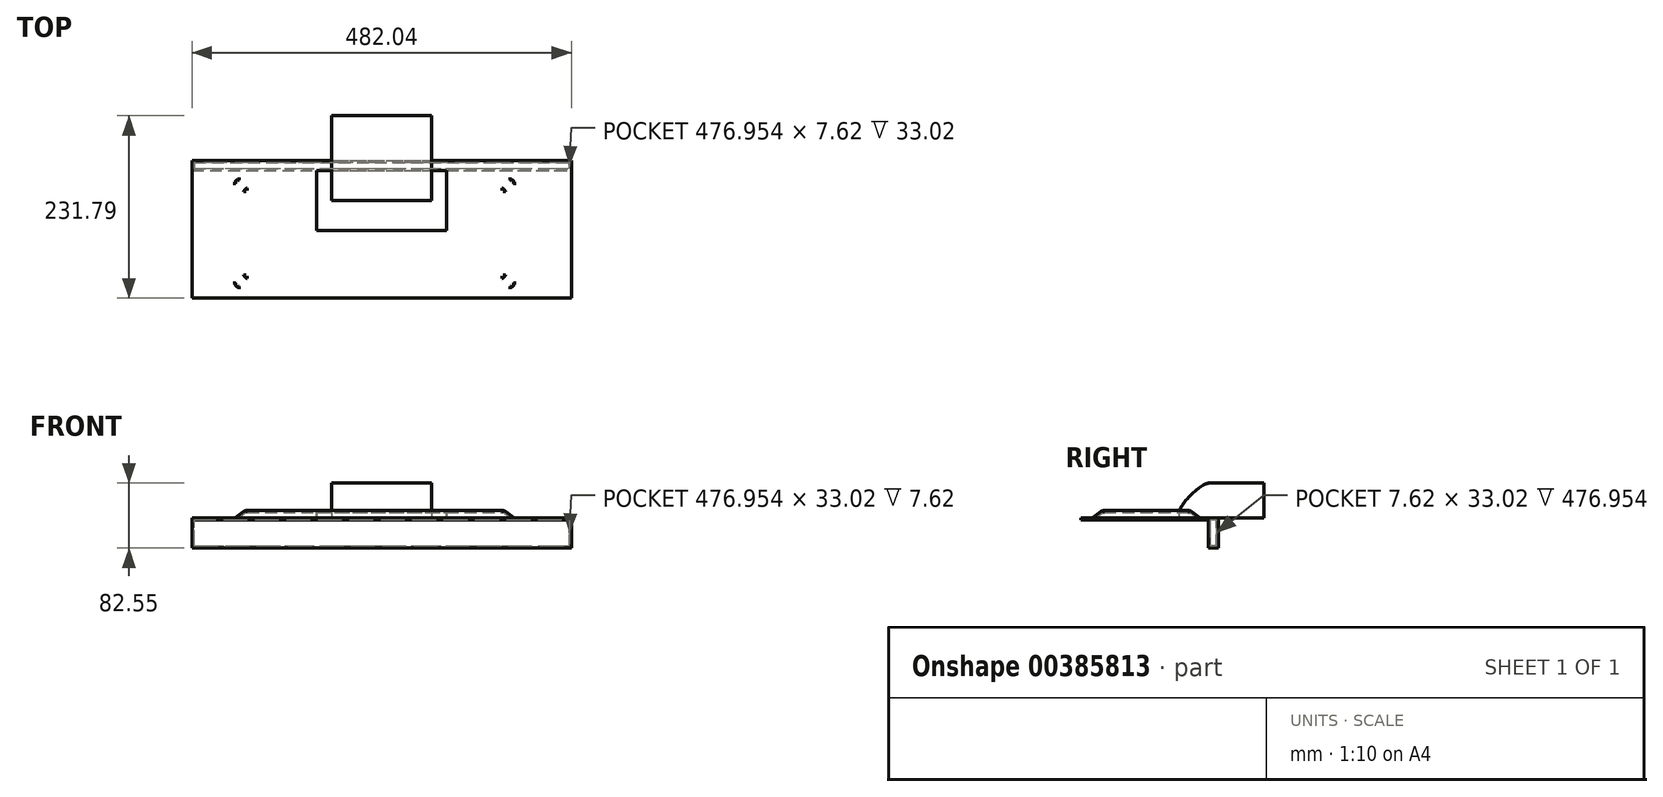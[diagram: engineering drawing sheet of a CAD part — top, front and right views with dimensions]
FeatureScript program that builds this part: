
annotation { "Feature Type Name" : "Feature", "Feature Type Description" : "" }
export const myFeature = defineFeature(function(context is Context, id is Id, definition is map)
    precondition{}
    {
        {
            var Q0;
            Q0=qCreatedBy(makeId("Top.planeOp"),FACE);
            var sketch = newSketch(context, id + "F0", { "sketchPlane" : qUnion([Q0])});
            skLineSegment(sketch, "E0", {"start": v(-241.02, 0) * mm, "end": v(241.02, 0) * mm});
            skLineSegment(sketch, "E1", {"start": v(-241.02, 0) * mm, "end": v(-241.02, -12.7) * mm});
            skLineSegment(sketch, "E2", {"start": v(-241.02, -12.7) * mm, "end": v(241.02, -12.7) * mm});
            skLineSegment(sketch, "E3", {"start": v(241.02, -12.7) * mm, "end": v(241.02, 0) * mm});
            skLineSegment(sketch, "E4", {"start": v(-82.55, -12.7) * mm, "end": v(-82.55, -88.9) * mm});
            skLineSegment(sketch, "E5", {"start": v(-82.55, -88.9) * mm, "end": v(82.55, -88.9) * mm});
            skLineSegment(sketch, "E6", {"start": v(82.55, -88.9) * mm, "end": v(82.55, -12.7) * mm});
            skLineSegment(sketch, "E7", {"start": v(0, -88.9) * mm, "end": v(0, 0) * mm, "construction": true});
            skLineSegment(sketch, "E8", {"start": v(241.02, -12.7) * mm, "end": v(241.02, -174.64) * mm});
            skLineSegment(sketch, "E9", {"start": v(-241.02, -12.7) * mm, "end": v(-241.02, -174.64) * mm});
            skLineSegment(sketch, "E10", {"start": v(-241.02, -174.64) * mm, "end": v(241.02, -174.64) * mm});
            skSolve(sketch);
        }
        {
            var Q0;
            Q0=makeQuery(id+"F0.imprint","IMPRINT",FACE,{"disambiguationData":[TD([[makeQuery(id+"F0.imprint","IMPRINT",EDGE,{"derivedFrom":sQuery(id+"F0.wireOp",EDGE,"E0")}),-1.0]])]});
            extrude(context, id + "F1", {"entities" : qUnion([Q0]), "oppositeDirection" : true, "depth" : 38.1 * mm});
        }
        {
            var Q0;
            {var subQ0=sQuery(id+"F0.wireOp",EDGE,"E4");Q0=makeQuery(id+"F0.imprint","IMPRINT",FACE,{"disambiguationData":[TD([[makeQuery(id+"F0.imprint","IMPRINT",EDGE,{"derivedFrom":subQ0}),-1.0]])]});}
            var Q1;
            {var subQ0=sQuery(id+"F0.wireOp",EDGE,"E4");Q1=makeQuery(id+"F0.imprint","IMPRINT",FACE,{"disambiguationData":[TD([[makeQuery(id+"F0.imprint","IMPRINT",EDGE,{"derivedFrom":subQ0}),1.0]])]});}
            extrude(context, id + "F2", {"entities" : qUnion([Q0, Q1]), "operationType" : NewBodyOperationType.ADD, "oppositeDirection" : true, "depth" : 2.54 * mm});
        }
        {
            var Q0;
            {var subQ0=sQuery(id+"F0.wireOp",EDGE,"E4");Q0=makeQuery(id+"F0.imprint","IMPRINT",FACE,{"disambiguationData":[TD([[makeQuery(id+"F0.imprint","IMPRINT",EDGE,{"derivedFrom":subQ0}),-1.0]])]});}
            var sketch = newSketch(context, id + "F3", { "sketchPlane" : qUnion([Q0])});
            skLineSegment(sketch, "E11.bottom", {"start": v(-186.92, -23) * mm, "end": v(169, -23) * mm});
            skLineSegment(sketch, "E11.top", {"start": v(-186.92, -161.38) * mm, "end": v(169, -161.38) * mm});
            skLineSegment(sketch, "E11.left", {"start": v(-186.92, -23) * mm, "end": v(-186.92, -161.38) * mm});
            skLineSegment(sketch, "E11.right", {"start": v(169, -23) * mm, "end": v(169, -161.38) * mm});
            skSolve(sketch);
        }
        {
            var Q0;
            Q0 = qSketchRegion(id + "F3", true);
            extrude(context, id + "F4", {"entities" : qUnion([Q0]), "operationType" : NewBodyOperationType.ADD, "depth" : 9.52 * mm});
        }
        {
            var Q0;
            Q0=makeQuery(id+"F4.opExtrude","CAP_EDGE",EDGE,{"disambiguationData":[OSD([sQuery(id+"F3.wireOp",EDGE,"E11.bottom")])],"isStart":false});
            var Q1;
            Q1=makeQuery(id+"F4.opExtrude","CAP_EDGE",EDGE,{"disambiguationData":[OSD([sQuery(id+"F3.wireOp",EDGE,"E11.right")])],"isStart":false});
            var Q2;
            Q2=makeQuery(id+"F4.opExtrude","CAP_EDGE",EDGE,{"disambiguationData":[OSD([sQuery(id+"F3.wireOp",EDGE,"E11.top")])],"isStart":false});
            var Q3;
            Q3=makeQuery(id+"F4.opExtrude","CAP_EDGE",EDGE,{"disambiguationData":[OSD([sQuery(id+"F3.wireOp",EDGE,"E11.left")])],"isStart":false});
            chamfer(context, id + "F5", {"entities" : qUnion([Q0, Q1, Q2, Q3]), "chamferType" : ChamferType.TWO_OFFSETS, "width1" : 9.52 * mm, "oppositeDirection" : false, "width2" : 13 * mm, "tangentPropagation" : true});
        }
        {
            var Q0;
            Q0=makeQuery(id+"F5.opChamfer","BLEND_EDGE",EDGE,{"blendedFrom":[makeQuery(id+"F4.opExtrude","CAP_EDGE",EDGE,{"disambiguationData":[OSD([sQuery(id+"F3.wireOp",EDGE,"E11.bottom")])],"isStart":false}),makeQuery(id+"F4.opExtrude","CAP_EDGE",EDGE,{"disambiguationData":[OSD([sQuery(id+"F3.wireOp",EDGE,"E11.right")])],"isStart":false})],"blendedInto":[]});
            var Q1;
            Q1=makeQuery(id+"F5.opChamfer","BLEND_EDGE",EDGE,{"blendedFrom":[makeQuery(id+"F4.opExtrude","CAP_EDGE",EDGE,{"disambiguationData":[OSD([sQuery(id+"F3.wireOp",EDGE,"E11.bottom")])],"isStart":false}),makeQuery(id+"F4.opExtrude","CAP_EDGE",EDGE,{"disambiguationData":[OSD([sQuery(id+"F3.wireOp",EDGE,"E11.left")])],"isStart":false})],"blendedInto":[]});
            var Q2;
            Q2=makeQuery(id+"F5.opChamfer","BLEND_EDGE",EDGE,{"blendedFrom":[makeQuery(id+"F4.opExtrude","CAP_EDGE",EDGE,{"disambiguationData":[OSD([sQuery(id+"F3.wireOp",EDGE,"E11.top")])],"isStart":false}),makeQuery(id+"F4.opExtrude","CAP_EDGE",EDGE,{"disambiguationData":[OSD([sQuery(id+"F3.wireOp",EDGE,"E11.left")])],"isStart":false})],"blendedInto":[]});
            var Q3;
            Q3=makeQuery(id+"F5.opChamfer","BLEND_EDGE",EDGE,{"blendedFrom":[makeQuery(id+"F4.opExtrude","CAP_EDGE",EDGE,{"disambiguationData":[OSD([sQuery(id+"F3.wireOp",EDGE,"E11.top")])],"isStart":false}),makeQuery(id+"F4.opExtrude","CAP_EDGE",EDGE,{"disambiguationData":[OSD([sQuery(id+"F3.wireOp",EDGE,"E11.right")])],"isStart":false})],"blendedInto":[]});
            fillet(context, id + "F6", {"entities" : qUnion([Q0, Q1, Q2, Q3]), "radius" : 7.62 * mm, "tangentPropagation" : true, "allowEdgeOverflow" : false});
        }
        {
            var Q0;
            {var subQ0=sQuery(id+"F3.wireOp",EDGE,"E11.top");Q0=makeQuery(id+"F5.opChamfer","BLEND_EDGE",EDGE,{"blendedFrom":[makeQuery(id+"F4.opExtrude","CAP_EDGE",EDGE,{"disambiguationData":[OSD([subQ0])],"isStart":false}),makeQuery(id+"F4.opExtrude","CAP_FACE",FACE,{"disambiguationData":[OSD([sQuery(id+"F3.wireOp",EDGE,"E11.bottom"),subQ0,sQuery(id+"F3.wireOp",EDGE,"E11.left"),sQuery(id+"F3.wireOp",EDGE,"E11.right")])],"isStart":false})],"blendedInto":[makeQuery(id+"F4.opExtrude","CAP_FACE",FACE,{"disambiguationData":[OSD([sQuery(id+"F3.wireOp",EDGE,"E11.bottom"),subQ0,sQuery(id+"F3.wireOp",EDGE,"E11.left"),sQuery(id+"F3.wireOp",EDGE,"E11.right")])],"isStart":false})]});}
            var Q1;
            {var subQ0=sQuery(id+"F0.wireOp",EDGE,"E2");Q1=makeQuery(id+"F5.opChamfer","BLEND_EDGE",EDGE,{"blendedFrom":[makeQuery(id+"F4.opExtrude","CAP_EDGE",EDGE,{"disambiguationData":[OSD([sQuery(id+"F3.wireOp",EDGE,"E11.top")])],"isStart":false}),makeQuery(id+"F2.boolean.opBoolean","MERGE",FACE,{"derivedFrom":[makeQuery(id+"F1.opExtrude","CAP_FACE",FACE,{"disambiguationData":[OSD([sQuery(id+"F0.wireOp",EDGE,"E0"),sQuery(id+"F0.wireOp",EDGE,"E1"),subQ0,sQuery(id+"F0.wireOp",EDGE,"E3")])],"isStart":true}),makeQuery(id+"F2.opExtrude","CAP_FACE",FACE,{"disambiguationData":[OSD([subQ0,sQuery(id+"F0.wireOp",EDGE,"E8"),sQuery(id+"F0.wireOp",EDGE,"E9"),sQuery(id+"F0.wireOp",EDGE,"E10")])],"isStart":true})]})],"blendedInto":[makeQuery(id+"F2.boolean.opBoolean","MERGE",FACE,{"derivedFrom":[makeQuery(id+"F1.opExtrude","CAP_FACE",FACE,{"disambiguationData":[OSD([sQuery(id+"F0.wireOp",EDGE,"E0"),sQuery(id+"F0.wireOp",EDGE,"E1"),subQ0,sQuery(id+"F0.wireOp",EDGE,"E3")])],"isStart":true}),makeQuery(id+"F2.opExtrude","CAP_FACE",FACE,{"disambiguationData":[OSD([subQ0,sQuery(id+"F0.wireOp",EDGE,"E8"),sQuery(id+"F0.wireOp",EDGE,"E9"),sQuery(id+"F0.wireOp",EDGE,"E10")])],"isStart":true})]})]});}
            fillet(context, id + "F7", {"entities" : qUnion([Q0, Q1]), "radius" : 5.08 * mm, "tangentPropagation" : true, "allowEdgeOverflow" : false});
        }
        {
            var Q0;
            {var subQ0=sQuery(id+"F0.wireOp",EDGE,"E4");Q0=makeQuery(id+"F0.imprint","IMPRINT",FACE,{"disambiguationData":[TD([[makeQuery(id+"F0.imprint","IMPRINT",EDGE,{"derivedFrom":subQ0}),1.0]])]});}
            extrude(context, id + "F8", {"entities" : qUnion([Q0]), "operationType" : NewBodyOperationType.REMOVE, "endBound" : BoundingType.THROUGH_ALL, "oppositeDirection" : true, "depth" : 25.4 * mm, "hasSecondDirection" : true, "secondDirectionBound" : SecondDirectionBoundingType.THROUGH_ALL, "secondDirectionOppositeDirection" : false, "secondDirectionDepth" : 25.4 * mm});
        }
        {
            var Q0;
            Q0=makeQuery(id+"F2.opExtrude","CAP_FACE",FACE,{"disambiguationData":[OSD([sQuery(id+"F0.wireOp",EDGE,"E2"),sQuery(id+"F0.wireOp",EDGE,"E8"),sQuery(id+"F0.wireOp",EDGE,"E9"),sQuery(id+"F0.wireOp",EDGE,"E10")])],"isStart":false});
            shell(context, id + "F9", {"entities" : qUnion([Q0]), "thickness" : 2.54 * mm});
        }
        {
            var Q0;
            Q0=makeQuery(id+"F9.opShell","OFFSET_FACE",FACE,{"disambiguationData":[OSD([sQuery(id+"F0.wireOp",EDGE,"E6")])]});
            var sketch = newSketch(context, id + "F10", { "sketchPlane" : qUnion([Q0])});
            skLineSegment(sketch, "E12.0", {"start": v(-91.44, -2.54) * mm, "end": v(-91.44, 6.99) * mm});
            skLineSegment(sketch, "E12.1", {"start": v(-91.44, 6.99) * mm, "end": v(-37.66, 6.99) * mm});
            skLineSegment(sketch, "E12.2", {"start": v(-91.44, -2.54) * mm, "end": v(-21.34, -2.54) * mm});
            skLineSegment(sketch, "E12.3", {"start": v(-36.16, 6.5) * mm, "end": v(-25.84, -1.07) * mm});
            skArc(sketch, "E12.4", {"start": v(-37.66, 6.99) * mm, "mid": v(-36.87, 6.86) * mm, "end": v(-36.16, 6.5) * mm});
            skArc(sketch, "E12.5", {"start": v(-21.34, -2.54) * mm, "mid": v(-23.7, -2.16) * mm, "end": v(-25.84, -1.07) * mm});
            skSolve(sketch);
        }
        {
            var Q0;
            Q0 = qSketchRegion(id + "F10", true);
            var Q1;
            Q1=makeQuery(id+"F9.opShell","OFFSET_FACE",FACE,{"disambiguationData":[OSD([sQuery(id+"F0.wireOp",EDGE,"E4")])]});
            extrude(context, id + "F11", {"entities" : qUnion([Q0]), "operationType" : NewBodyOperationType.REMOVE, "endBound" : BoundingType.UP_TO_SURFACE, "oppositeDirection" : true, "endBoundEntityFace" : qUnion([Q1]), "depth" : 25.4 * mm});
        }
        {
            var Q0;
            Q0=qCreatedBy(makeId("Top.planeOp"),FACE);
            var sketch = newSketch(context, id + "F12", { "sketchPlane" : qUnion([Q0])});
            skLineSegment(sketch, "E13.bottom", {"start": v(-63.5, 57.15) * mm, "end": v(63.5, 57.15) * mm});
            skLineSegment(sketch, "E13.top", {"start": v(-63.5, -50.8) * mm, "end": v(63.5, -50.8) * mm});
            skLineSegment(sketch, "E13.left", {"start": v(-63.5, 57.15) * mm, "end": v(-63.5, -50.8) * mm});
            skLineSegment(sketch, "E13.right", {"start": v(63.5, 57.15) * mm, "end": v(63.5, -50.8) * mm});
            skLineSegment(sketch, "E14", {"start": v(0, -50.8) * mm, "end": v(0, 0) * mm, "construction": true});
            skSolve(sketch);
        }
        {
            var Q0;
            Q0 = qSketchRegion(id + "F12", true);
            extrude(context, id + "F13", {"entities" : qUnion([Q0]), "operationType" : NewBodyOperationType.ADD, "depth" : 44.45 * mm});
        }
        {
            var Q0;
            Q0=makeQuery(id+"F13.opExtrude","CAP_EDGE",EDGE,{"disambiguationData":[OSD([sQuery(id+"F12.wireOp",EDGE,"E13.top")])],"isStart":false});
            fillet(context, id + "F14", {"entities" : qUnion([Q0]), "radius" : 38.1 * mm, "tangentPropagation" : true, "rho" : .2, "crossSection" : FilletCrossSection.CONIC, "allowEdgeOverflow" : false});
        }
    });
